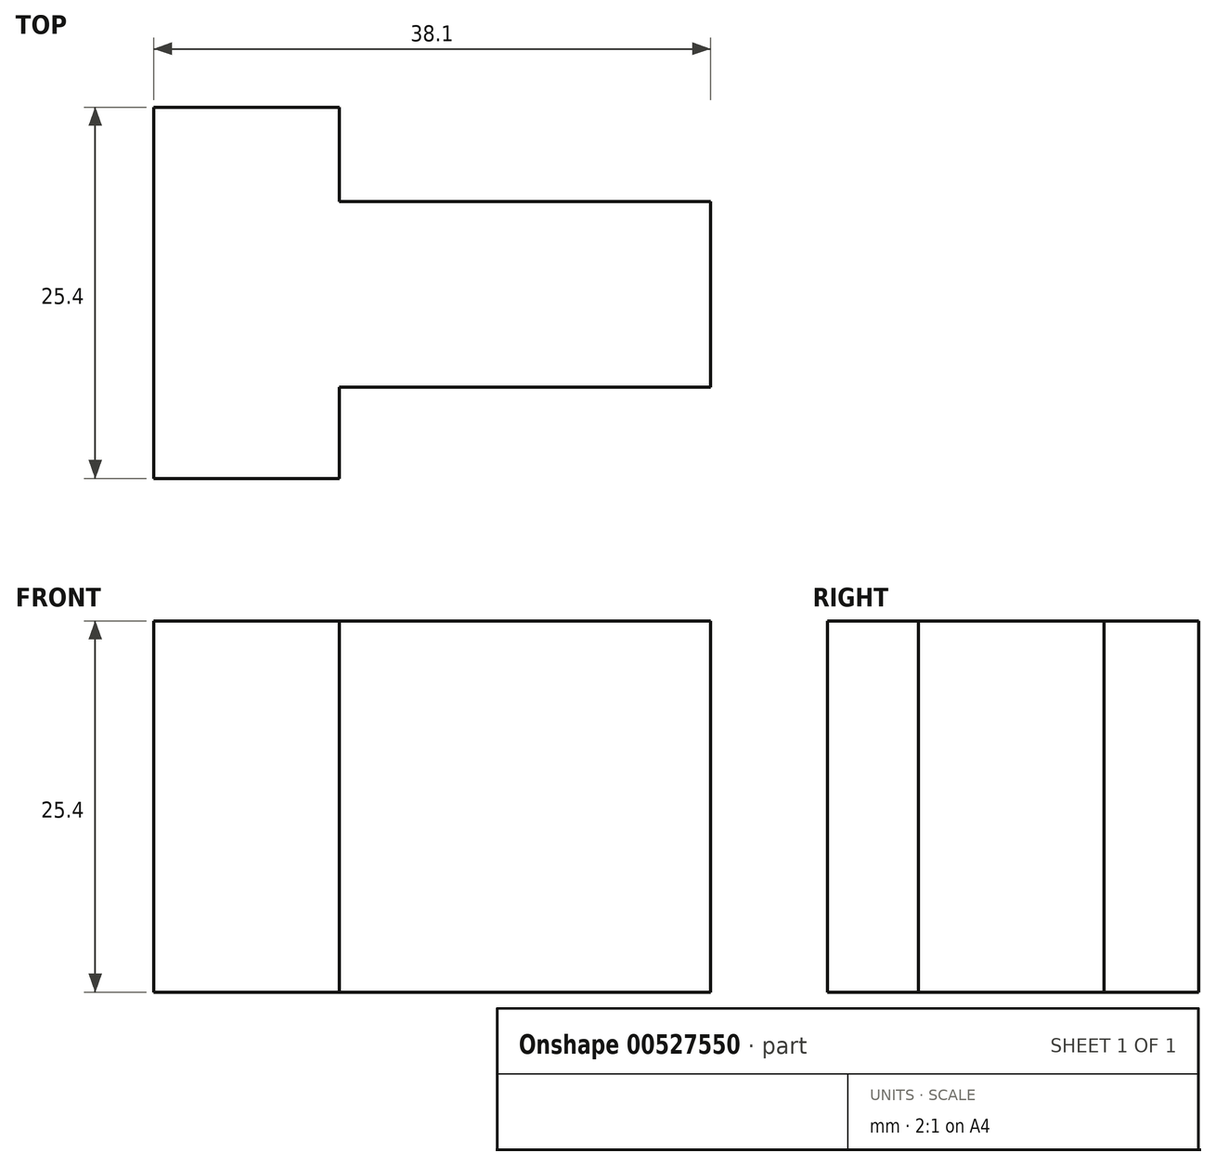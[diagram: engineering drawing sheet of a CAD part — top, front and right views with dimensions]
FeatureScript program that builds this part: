
annotation { "Feature Type Name" : "Feature", "Feature Type Description" : "" }
export const myFeature = defineFeature(function(context is Context, id is Id, definition is map)
    precondition{}
    {
        {
            var Q0;
            Q0=qCreatedBy(makeId("Top.planeOp"),FACE);
            var sketch = newSketch(context, id + "F0", { "sketchPlane" : qUnion([Q0])});
            skLineSegment(sketch, "E0", {"start": v(0, 0) * mm, "end": v(0, 25.4) * mm});
            skLineSegment(sketch, "E1", {"start": v(0, 25.4) * mm, "end": v(12.7, 25.4) * mm});
            skLineSegment(sketch, "E2", {"start": v(12.7, 25.4) * mm, "end": v(12.7, 18.93) * mm});
            skLineSegment(sketch, "E3", {"start": v(12.7, 18.93) * mm, "end": v(38.1, 18.93) * mm});
            skLineSegment(sketch, "E4", {"start": v(0, 0) * mm, "end": v(12.7, 0) * mm});
            skLineSegment(sketch, "E5", {"start": v(12.7, 0) * mm, "end": v(12.7, 6.23) * mm});
            skLineSegment(sketch, "E6", {"start": v(12.7, 6.23) * mm, "end": v(38.1, 6.23) * mm});
            skLineSegment(sketch, "E7", {"start": v(38.1, 6.23) * mm, "end": v(38.1, 18.93) * mm});
            skSolve(sketch);
        }
        {
            var Q0;
            Q0=makeQuery(id+"F0.imprint","IMPRINT",FACE,{"disambiguationData":[TD([[makeQuery(id+"F0.imprint","IMPRINT",EDGE,{"derivedFrom":sQuery(id+"F0.wireOp",EDGE,"E0")}),-1.0]])]});
            extrude(context, id + "F1", {"entities" : qUnion([Q0]), "depth" : 25.4 * mm, "offsetDistance" : 25.4 * mm});
        }
    });
